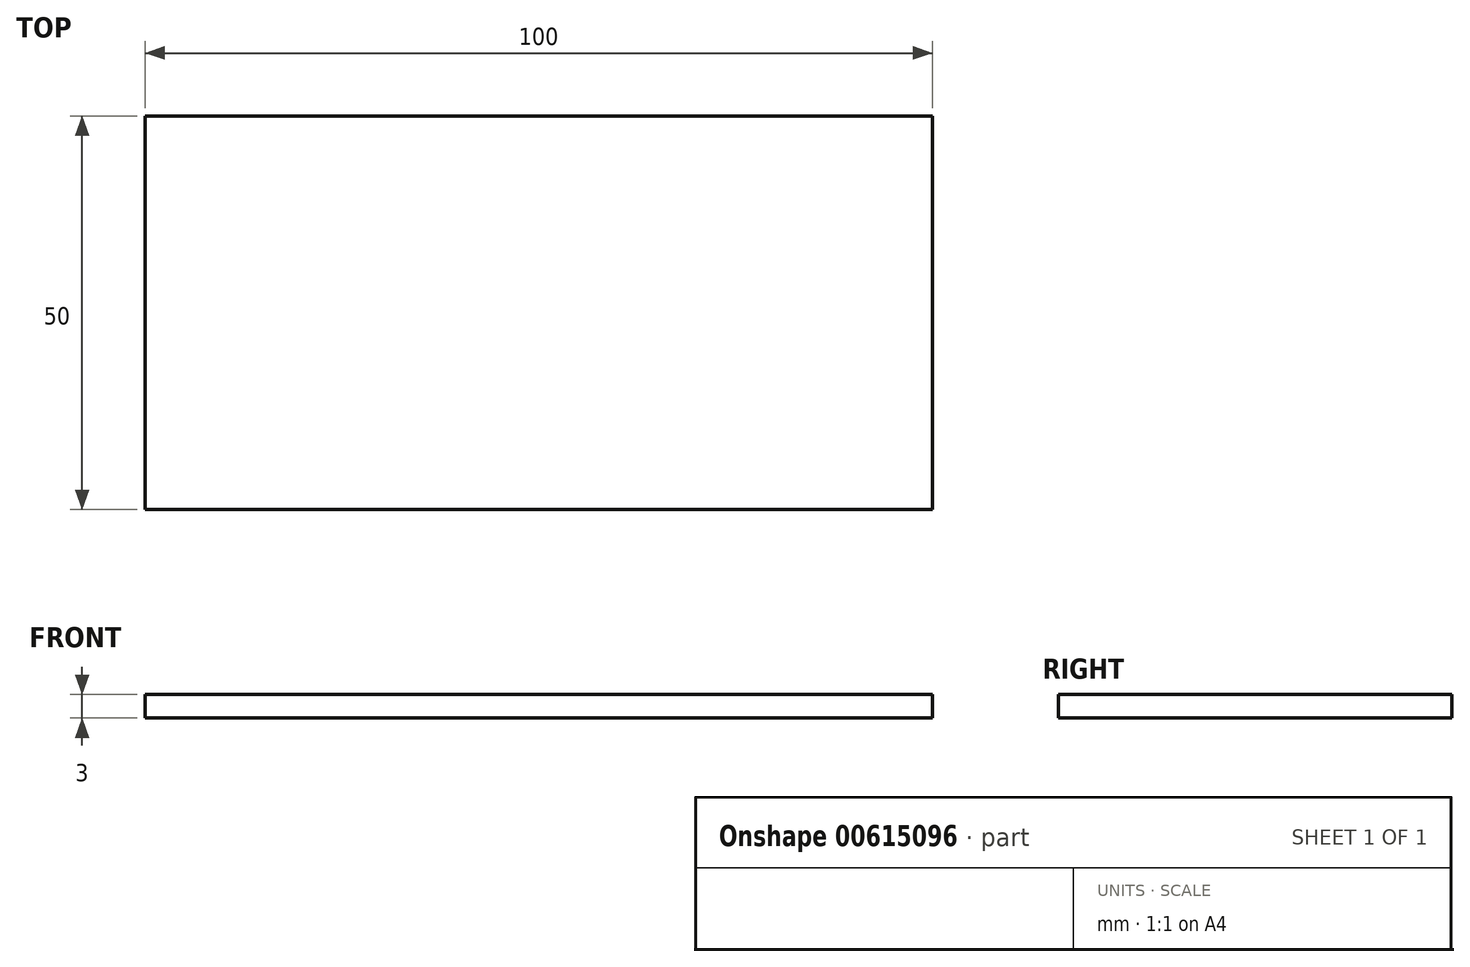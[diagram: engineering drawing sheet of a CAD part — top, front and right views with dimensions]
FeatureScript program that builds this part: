
annotation { "Feature Type Name" : "Feature", "Feature Type Description" : "" }
export const myFeature = defineFeature(function(context is Context, id is Id, definition is map)
    precondition{}
    {
        {
            var Q0;
            Q0=qCreatedBy(makeId("Top.planeOp"),FACE);
            var sketch = newSketch(context, id + "F0", { "sketchPlane" : qUnion([Q0])});
            skLineSegment(sketch, "E0.bottom", {"start": v(0, 0) * mm, "end": v(100, 0) * mm});
            skLineSegment(sketch, "E0.top", {"start": v(0, 50) * mm, "end": v(100, 50) * mm});
            skLineSegment(sketch, "E0.left", {"start": v(0, 0) * mm, "end": v(0, 50) * mm});
            skLineSegment(sketch, "E0.right", {"start": v(100, 0) * mm, "end": v(100, 50) * mm});
            skSolve(sketch);
        }
        {
            var Q0;
            Q0 = qSketchRegion(id + "F0", true);
            extrude(context, id + "F1", {"entities" : qUnion([Q0]), "depth" : 3 * mm, "offsetDistance" : 25 * mm});
        }
    });
